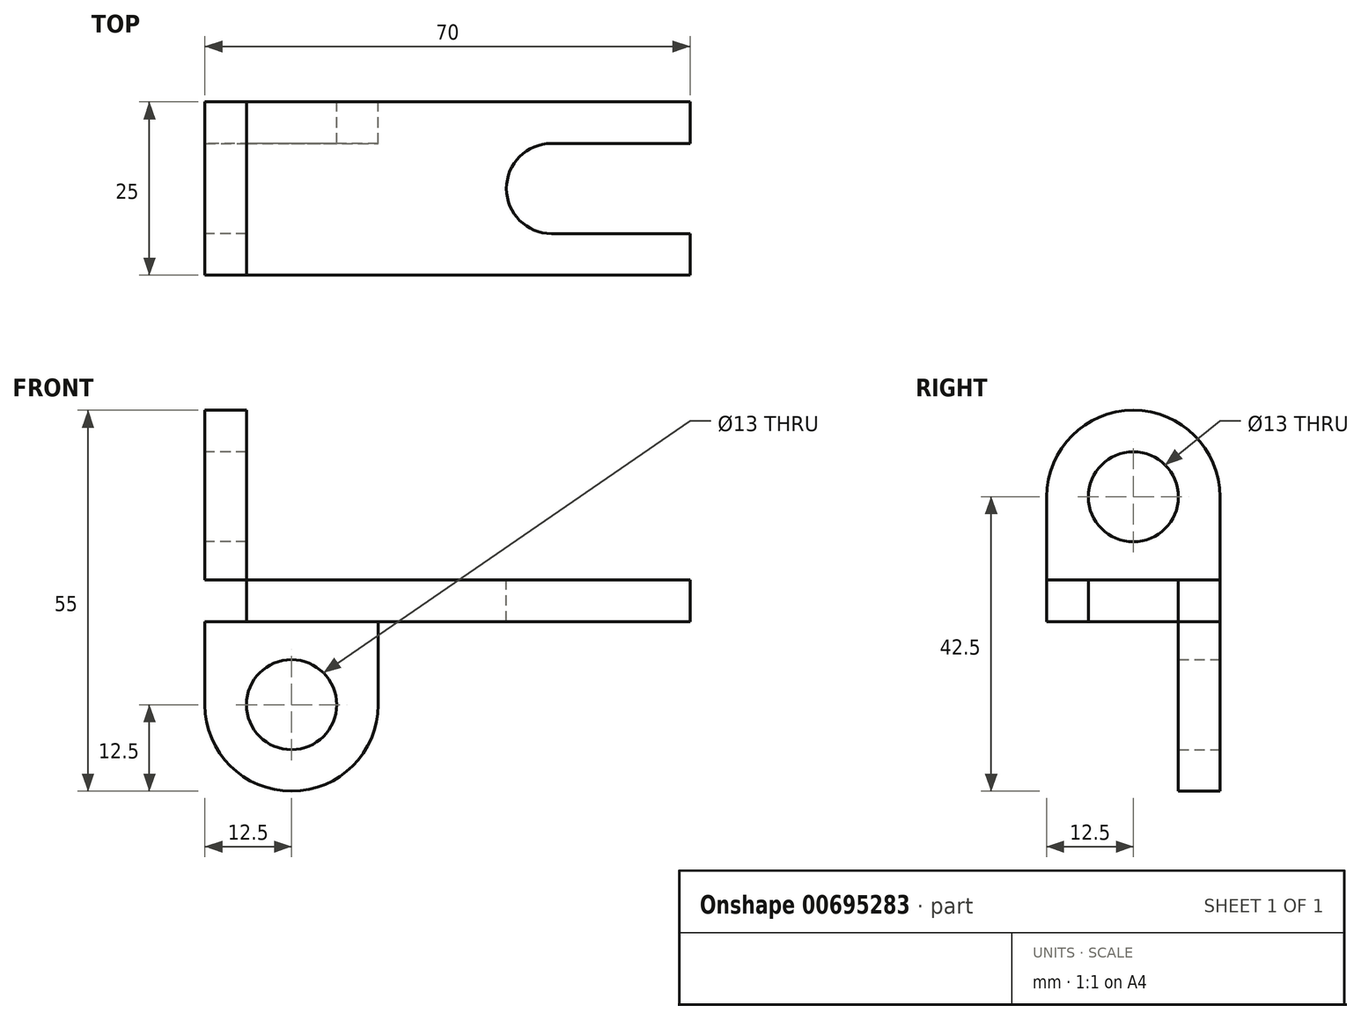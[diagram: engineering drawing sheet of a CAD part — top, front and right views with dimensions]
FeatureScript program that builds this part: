
annotation { "Feature Type Name" : "Feature", "Feature Type Description" : "" }
export const myFeature = defineFeature(function(context is Context, id is Id, definition is map)
    precondition{}
    {
        {
            var Q0;
            Q0=qCreatedBy(makeId("Front.planeOp"),FACE);
            var sketch = newSketch(context, id + "F0", { "sketchPlane" : qUnion([Q0])});
            skLineSegment(sketch, "E0.bottom", {"start": v(-32, 3) * mm, "end": v(32, 3) * mm});
            skLineSegment(sketch, "E0.top", {"start": v(-32, -3) * mm, "end": v(32, -3) * mm});
            skLineSegment(sketch, "E0.left", {"start": v(-32, 3) * mm, "end": v(-32, -3) * mm});
            skLineSegment(sketch, "E0.right", {"start": v(32, 3) * mm, "end": v(32, -3) * mm});
            skPoint(sketch, "E0.middle", {"position": v(0, 0) * mm});
            skSolve(sketch);
        }
        {
            var Q0;
            Q0=makeQuery(id+"F0.imprint","IMPRINT",FACE,{"disambiguationData":[TD([[makeQuery(id+"F0.imprint","IMPRINT",EDGE,{"derivedFrom":sQuery(id+"F0.wireOp",EDGE,"E0.bottom")}),-1.0]])]});
            extrude(context, id + "F1", {"entities" : qUnion([Q0]), "depth" : 25 * mm, "offsetDistance" : 25 * mm});
        }
        {
            var Q0;
            Q0=makeQuery(id+"F1.opExtrude","SWEPT_FACE",FACE,{"disambiguationData":[OSD([sQuery(id+"F0.wireOp",EDGE,"E0.bottom")])]});
            var sketch = newSketch(context, id + "F2", { "sketchPlane" : qUnion([Q0])});
            skLineSegment(sketch, "E1.bottom", {"start": v(32, -6) * mm, "end": v(12, -6) * mm});
            skLineSegment(sketch, "E1.top", {"start": v(32, -19) * mm, "end": v(12, -19) * mm});
            skLineSegment(sketch, "E1.left", {"start": v(32, -6) * mm, "end": v(32, -19) * mm});
            skLineSegment(sketch, "E1.right", {"start": v(12, -6) * mm, "end": v(12, -19) * mm});
            skCircle(sketch, "E2", {"center": v(12, -12.5) * mm, "radius": 6.5 * mm});
            skSolve(sketch);
        }
        {
            var Q0;
            {var subQ0=sQuery(id+"F2.wireOp",EDGE,"E1.right");Q0=makeQuery(id+"F2.imprint","IMPRINT",FACE,{"disambiguationData":[TD([[makeQuery(id+"F2.imprint","IMPRINT",EDGE,{"derivedFrom":subQ0}),-1.0]])]});}
            var Q1;
            {var subQ0=sQuery(id+"F2.wireOp",EDGE,"E1.right");Q1=makeQuery(id+"F2.imprint","IMPRINT",FACE,{"disambiguationData":[TD([[makeQuery(id+"F2.imprint","IMPRINT",EDGE,{"derivedFrom":subQ0}),1.0]])]});}
            var Q2;
            {var subQ0=sQuery(id+"F2.wireOp",EDGE,"E1.bottom");Q2=makeQuery(id+"F2.imprint","IMPRINT",FACE,{"disambiguationData":[TD([[makeQuery(id+"F2.imprint","IMPRINT",EDGE,{"derivedFrom":subQ0}),1.0]])]});}
            extrude(context, id + "F3", {"entities" : qUnion([Q0, Q1, Q2]), "operationType" : NewBodyOperationType.REMOVE, "oppositeDirection" : true, "depth" : 10.9 * mm, "offsetDistance" : 25 * mm});
        }
        {
            var Q0;
            Q0=qCreatedBy(makeId("Front.planeOp"),FACE);
            var sketch = newSketch(context, id + "F4", { "sketchPlane" : qUnion([Q0])});
            skLineSegment(sketch, "E3.bottom", {"start": v(-32, 3) * mm, "end": v(-38, 3) * mm});
            skLineSegment(sketch, "E3.top", {"start": v(-32, 27.5) * mm, "end": v(-38, 27.5) * mm});
            skLineSegment(sketch, "E3.left", {"start": v(-32, 3) * mm, "end": v(-32, 27.5) * mm});
            skLineSegment(sketch, "E3.right", {"start": v(-38, 3) * mm, "end": v(-38, 27.5) * mm});
            skLineSegment(sketch, "E4.bottom", {"start": v(-38, 3) * mm, "end": v(-32, 3) * mm});
            skLineSegment(sketch, "E4.top", {"start": v(-38, -3) * mm, "end": v(-32, -3) * mm});
            skLineSegment(sketch, "E4.left", {"start": v(-38, 3) * mm, "end": v(-38, -3) * mm});
            skLineSegment(sketch, "E4.right", {"start": v(-32, 3) * mm, "end": v(-32, -3) * mm});
            skSolve(sketch);
        }
        {
            var Q0;
            Q0=makeQuery(id+"F4.imprint","IMPRINT",FACE,{"disambiguationData":[TD([[makeQuery(id+"F4.imprint","IMPRINT",EDGE,{"derivedFrom":sQuery(id+"F4.wireOp",EDGE,"E3.top")}),1.0]])]});
            var Q1;
            Q1=makeQuery(id+"F4.imprint","IMPRINT",FACE,{"disambiguationData":[TD([[makeQuery(id+"F4.imprint","IMPRINT",EDGE,{"derivedFrom":sQuery(id+"F4.wireOp",EDGE,"E4.bottom")}),-1.0]])]});
            extrude(context, id + "F5", {"entities" : qUnion([Q0, Q1]), "operationType" : NewBodyOperationType.ADD, "depth" : 25 * mm, "offsetDistance" : 25 * mm});
        }
        {
            var Q0;
            Q0=makeQuery(id+"F5.opExtrude","SWEPT_FACE",FACE,{"disambiguationData":[OSD([sQuery(id+"F4.wireOp",EDGE,"E3.right"),sQuery(id+"F4.wireOp",EDGE,"E4.left")])]});
            var sketch = newSketch(context, id + "F6", { "sketchPlane" : qUnion([Q0])});
            skCircle(sketch, "E5", {"center": v(12.5, 15) * mm, "radius": 12.5 * mm});
            skCircle(sketch, "E6", {"center": v(12.5, 15) * mm, "radius": 6.5 * mm});
            skSolve(sketch);
        }
        {
            var Q0;
            {var subQ0=sQuery(id+"F6.wireOp",EDGE,"E5");var subQ1=sQuery(id+"F4.wireOp",EDGE,"E3.right");var subQ2=makeQuery(id+"F5.opExtrude","SWEPT_EDGE",EDGE,{"disambiguationData":[OSD([sQuery(id+"F4.wireOp",EDGE,"E3.top"),subQ1])]});var subQ3=makeQuery(id+"F6.imprint","INTERSECT",VERTEX,{"derivedFrom":[subQ2,subQ0]});Q0=makeQuery(id+"F6.imprint","IMPRINT",FACE,{"disambiguationData":[TD([[makeQuery(id+"F6.imprint","IMPRINT",EDGE,{"disambiguationData":[TD([[subQ3,-1.0]])],"derivedFrom":subQ0}),-1.0]])]});}
            var Q1;
            {var subQ0=sQuery(id+"F6.wireOp",EDGE,"E5");var subQ1=sQuery(id+"F4.wireOp",EDGE,"E3.right");var subQ2=makeQuery(id+"F5.opExtrude","SWEPT_EDGE",EDGE,{"disambiguationData":[OSD([sQuery(id+"F4.wireOp",EDGE,"E3.top"),subQ1])]});var subQ3=makeQuery(id+"F6.imprint","INTERSECT",VERTEX,{"derivedFrom":[subQ2,subQ0]});Q1=makeQuery(id+"F6.imprint","IMPRINT",FACE,{"disambiguationData":[TD([[makeQuery(id+"F6.imprint","IMPRINT",EDGE,{"disambiguationData":[TD([[subQ3,1.0]])],"derivedFrom":subQ0}),-1.0]])]});}
            var Q2;
            Q2=makeQuery(id+"F6.imprint","IMPRINT",FACE,{"disambiguationData":[TD([[makeQuery(id+"F6.imprint","IMPRINT",EDGE,{"derivedFrom":sQuery(id+"F6.wireOp",EDGE,"E6")}),1.0]])]});
            extrude(context, id + "F7", {"entities" : qUnion([Q0, Q1, Q2]), "operationType" : NewBodyOperationType.REMOVE, "oppositeDirection" : true, "depth" : 10 * mm, "offsetDistance" : 25 * mm});
        }
        {
            var Q0;
            Q0=makeQuery(id+"F5.boolean.opBoolean","MERGE",FACE,{"derivedFrom":[makeQuery(id+"F1.opExtrude","CAP_FACE",FACE,{"disambiguationData":[OSD([sQuery(id+"F0.wireOp",EDGE,"E0.bottom"),sQuery(id+"F0.wireOp",EDGE,"E0.top"),sQuery(id+"F0.wireOp",EDGE,"E0.left"),sQuery(id+"F0.wireOp",EDGE,"E0.right")])],"isStart":true}),makeQuery(id+"F5.opExtrude","CAP_FACE",FACE,{"disambiguationData":[OSD([sQuery(id+"F4.wireOp",EDGE,"E3.top"),sQuery(id+"F4.wireOp",EDGE,"E3.left"),sQuery(id+"F4.wireOp",EDGE,"E3.right"),sQuery(id+"F4.wireOp",EDGE,"E4.top"),sQuery(id+"F4.wireOp",EDGE,"E4.left"),sQuery(id+"F4.wireOp",EDGE,"E4.right")])],"isStart":true})]});
            var sketch = newSketch(context, id + "F8", { "sketchPlane" : qUnion([Q0])});
            skLineSegment(sketch, "E7.bottom", {"start": v(38, -3) * mm, "end": v(13, -3) * mm});
            skLineSegment(sketch, "E7.top", {"start": v(38, -27.5) * mm, "end": v(13, -27.5) * mm});
            skLineSegment(sketch, "E7.left", {"start": v(38, -3) * mm, "end": v(38, -27.5) * mm});
            skLineSegment(sketch, "E7.right", {"start": v(13, -3) * mm, "end": v(13, -27.5) * mm});
            skSolve(sketch);
        }
        {
            var Q0;
            Q0=makeQuery(id+"F8.imprint","IMPRINT",FACE,{"disambiguationData":[TD([[makeQuery(id+"F8.imprint","IMPRINT",EDGE,{"derivedFrom":sQuery(id+"F8.wireOp",EDGE,"E7.bottom")}),1.0]])]});
            extrude(context, id + "F9", {"entities" : qUnion([Q0]), "operationType" : NewBodyOperationType.ADD, "depth" : -6 * mm, "offsetDistance" : 25 * mm});
        }
        {
            var Q0;
            Q0=makeQuery(id+"F9.boolean.opBoolean","MERGE",FACE,{"derivedFrom":[makeQuery(id+"F5.boolean.opBoolean","MERGE",FACE,{"derivedFrom":[makeQuery(id+"F1.opExtrude","CAP_FACE",FACE,{"disambiguationData":[OSD([sQuery(id+"F0.wireOp",EDGE,"E0.bottom"),sQuery(id+"F0.wireOp",EDGE,"E0.top"),sQuery(id+"F0.wireOp",EDGE,"E0.left"),sQuery(id+"F0.wireOp",EDGE,"E0.right")])],"isStart":true}),makeQuery(id+"F5.opExtrude","CAP_FACE",FACE,{"disambiguationData":[OSD([sQuery(id+"F4.wireOp",EDGE,"E3.top"),sQuery(id+"F4.wireOp",EDGE,"E3.left"),sQuery(id+"F4.wireOp",EDGE,"E3.right"),sQuery(id+"F4.wireOp",EDGE,"E4.top"),sQuery(id+"F4.wireOp",EDGE,"E4.left"),sQuery(id+"F4.wireOp",EDGE,"E4.right")])],"isStart":true})]}),makeQuery(id+"F9.opExtrude","CAP_FACE",FACE,{"disambiguationData":[OSD([sQuery(id+"F8.wireOp",EDGE,"E7.bottom"),sQuery(id+"F8.wireOp",EDGE,"E7.top"),sQuery(id+"F8.wireOp",EDGE,"E7.left"),sQuery(id+"F8.wireOp",EDGE,"E7.right")])],"isStart":true})]});
            var sketch = newSketch(context, id + "F10", { "sketchPlane" : qUnion([Q0])});
            skCircle(sketch, "E8", {"center": v(25.5, -15) * mm, "radius": 12.5 * mm});
            skCircle(sketch, "E9", {"center": v(25.5, -15) * mm, "radius": 6.5 * mm});
            skSolve(sketch);
        }
        {
            var Q0;
            {var subQ0=sQuery(id+"F10.wireOp",EDGE,"E8");var subQ1=makeQuery(id+"F9.opExtrude","CAP_EDGE",EDGE,{"disambiguationData":[OSD([sQuery(id+"F8.wireOp",EDGE,"E7.right")])],"isStart":true});var subQ2=makeQuery(id+"F10.imprint","INTERSECT",VERTEX,{"derivedFrom":[subQ1,subQ0]});Q0=makeQuery(id+"F10.imprint","IMPRINT",FACE,{"disambiguationData":[TD([[makeQuery(id+"F10.imprint","IMPRINT",EDGE,{"disambiguationData":[TD([[subQ2,-1.0]])],"derivedFrom":subQ0}),-1.0]])]});}
            var Q1;
            {var subQ0=sQuery(id+"F10.wireOp",EDGE,"E8");var subQ3=makeQuery(id+"F9.opExtrude","CAP_EDGE",EDGE,{"disambiguationData":[OSD([sQuery(id+"F8.wireOp",EDGE,"E7.top")])],"isStart":true});var subQ4=makeQuery(id+"F10.imprint","INTERSECT",VERTEX,{"derivedFrom":[subQ3,subQ0]});Q1=makeQuery(id+"F10.imprint","IMPRINT",FACE,{"disambiguationData":[TD([[makeQuery(id+"F10.imprint","IMPRINT",EDGE,{"disambiguationData":[TD([[subQ4,-1.0]])],"derivedFrom":subQ0}),-1.0]])]});}
            var Q2;
            Q2=makeQuery(id+"F10.imprint","IMPRINT",FACE,{"disambiguationData":[TD([[makeQuery(id+"F10.imprint","IMPRINT",EDGE,{"derivedFrom":sQuery(id+"F10.wireOp",EDGE,"E9")}),1.0]])]});
            extrude(context, id + "F11", {"entities" : qUnion([Q0, Q1, Q2]), "operationType" : NewBodyOperationType.REMOVE, "oppositeDirection" : true, "depth" : 25 * mm, "offsetDistance" : 25 * mm});
        }
    });
